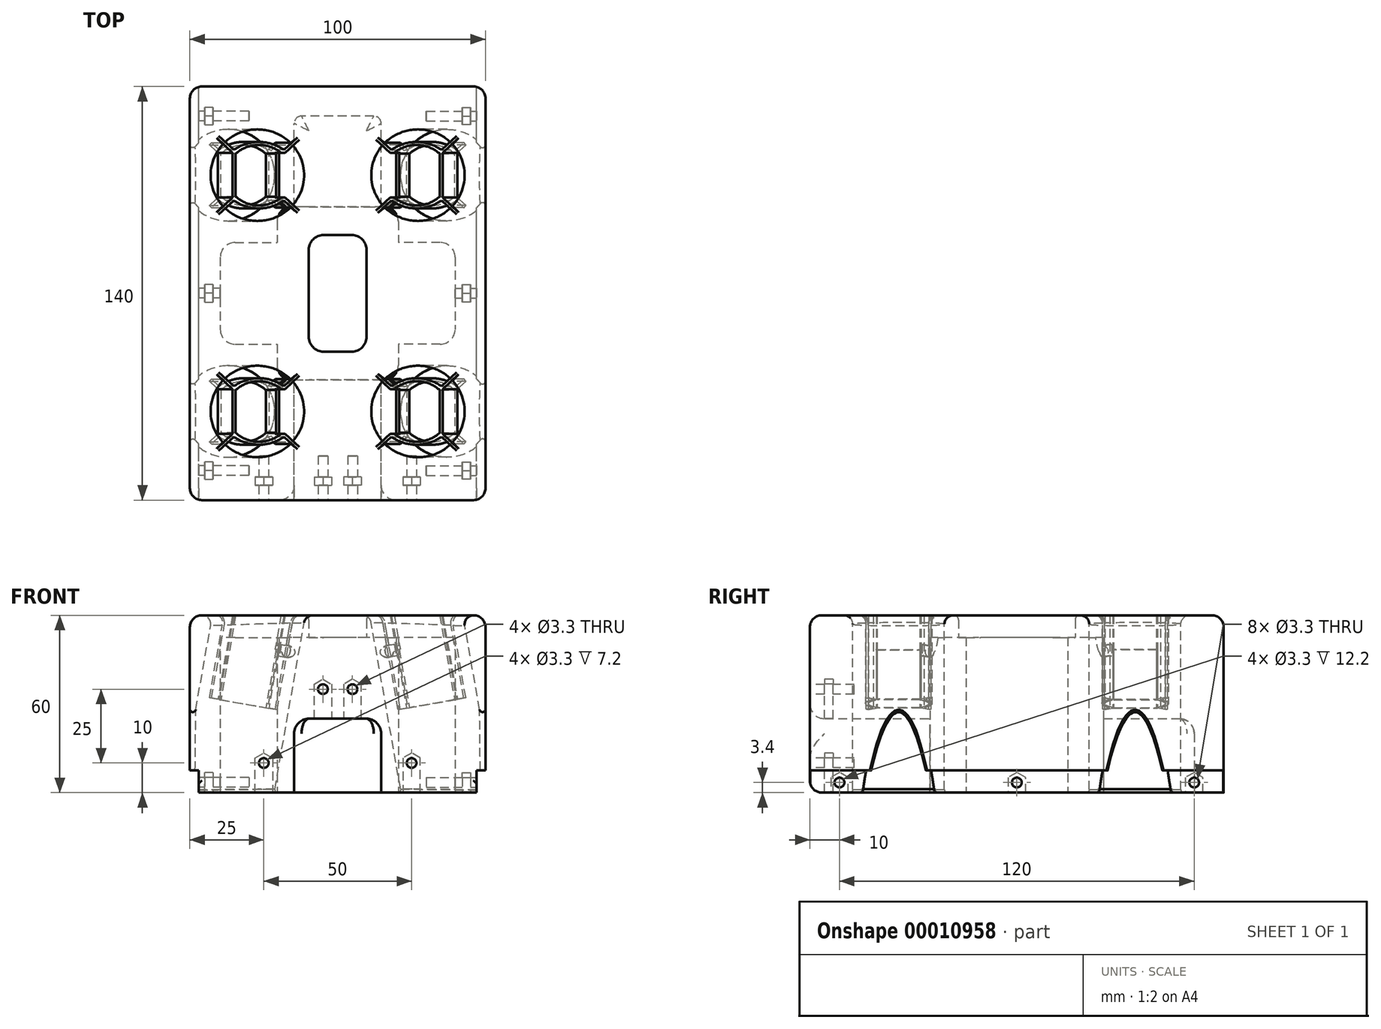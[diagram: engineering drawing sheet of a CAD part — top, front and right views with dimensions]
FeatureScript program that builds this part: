
annotation { "Feature Type Name" : "Feature", "Feature Type Description" : "" }
export const myFeature = defineFeature(function(context is Context, id is Id, definition is map)
    precondition{}
    {
        {
            var Q0;
            Q0=qCreatedBy(makeId("Right.planeOp"),FACE);
            var sketch = newSketch(context, id + "F0", { "sketchPlane" : qUnion([Q0])});
            skLineSegment(sketch, "E0", {"start": v(-70, 30) * mm, "end": v(70, 30) * mm});
            skLineSegment(sketch, "E1", {"start": v(70, 30) * mm, "end": v(70, -30) * mm});
            skLineSegment(sketch, "E2", {"start": v(70, -30) * mm, "end": v(-70, -30) * mm});
            skLineSegment(sketch, "E3", {"start": v(-70, -30) * mm, "end": v(-70, 0) * mm});
            skLineSegment(sketch, "E4", {"start": v(-70, 0) * mm, "end": v(-70, 0) * mm});
            skLineSegment(sketch, "E5", {"start": v(-70, 0) * mm, "end": v(-70, 30) * mm});
            skLineSegment(sketch, "E6", {"start": v(-70, 0) * mm, "end": v(70, 0) * mm, "construction": true});
            skSolve(sketch);
        }
        {
            var Q0;
            Q0=qSketchRegion(id+"F0",true);
            extrude(context, id + "F1", {"entities" : qUnion([Q0]), "depth" : 50 * mm});
        }
        {
            var Q0;
            Q0=qCreatedBy(makeId("Front.planeOp"),FACE);
            var sketch = newSketch(context, id + "F2", { "sketchPlane" : qUnion([Q0])});
            skLineSegment(sketch, "E7", {"start": v(25, -30) * mm, "end": v(25, 30) * mm, "construction": true});
            skLineSegment(sketch, "E8", {"start": v(50, 30) * mm, "end": v(0, 38.82) * mm, "construction": true});
            skLineSegment(sketch, "E9", {"start": v(0, 38.82) * mm, "end": v(-5.12, 9.78) * mm, "construction": true});
            skSolve(sketch);
        }
        {
            var Q0;
            Q0=sQuery(id+"F2.wireOp",EDGE,"E9");
            var Q1;
            Q1=sQuery(id+"F2.wireOp",VERTEX,"E8.end");
            cPlane(context, id + "F3", {"entities" : qUnion([Q0, Q1]), "cplaneType" : CPlaneType.LINE_POINT, "offset" : 150 * mm, "width" : 150 * mm, "height" : 150 * mm});
        }
        {
            var Q0;
            Q0=qCreatedBy(id+"F3.planeOp",FACE);
            cPlane(context, id + "F4", {"entities" : qUnion([Q0]), "cplaneType" : CPlaneType.OFFSET, "offset" : 35 * mm, "width" : 150 * mm, "height" : 150 * mm});
        }
        {
            var Q0;
            Q0=qCreatedBy(id+"F4.planeOp",FACE);
            cPlane(context, id + "F5", {"entities" : qUnion([Q0]), "cplaneType" : CPlaneType.OFFSET, "offset" : 20 * mm, "oppositeDirection" : true, "width" : 150 * mm, "height" : 150 * mm});
        }
        {
            var Q0;
            Q0=qCreatedBy(id+"F3.planeOp",FACE);
            var sketch = newSketch(context, id + "F6", { "sketchPlane" : qUnion([Q0])});
            skCircle(sketch, "E10", {"center": v(17.8, -40) * mm, "radius": 15.5 * mm});
            skCircle(sketch, "E11", {"center": v(17.8, 40) * mm, "radius": 15.5 * mm});
            skLineSegment(sketch, "E12", {"start": v(17.8, -40) * mm, "end": v(17.8, 40) * mm, "construction": true});
            skLineSegment(sketch, "E13", {"start": v(17.8, -40) * mm, "end": v(17.8, -70) * mm, "construction": true});
            skLineSegment(sketch, "E14", {"start": v(17.8, 40) * mm, "end": v(17.8, 70) * mm, "construction": true});
            skSolve(sketch);
        }
        {
            var Q0;
            Q0=qSketchRegion(id+"F6",true);
            extrude(context, id + "F7", {"entities" : qUnion([Q0]), "operationType" : NewBodyOperationType.REMOVE, "endBound" : BoundingType.THROUGH_ALL, "depth" : 25 * mm});
        }
        {
            var Q0;
            Q0=makeQuery(id+"F7.boolean.opBoolean","INTERSECT",EDGE,{"derivedFrom":[makeQuery(id+"F1.opExtrude","CAP_FACE",FACE,{"disambiguationData":[OSD([sQuery(id+"F0.wireOp",EDGE,"E0"),sQuery(id+"F0.wireOp",EDGE,"E1"),sQuery(id+"F0.wireOp",EDGE,"E2"),sQuery(id+"F0.wireOp",EDGE,"E3"),sQuery(id+"F0.wireOp",EDGE,"E4"),sQuery(id+"F0.wireOp",EDGE,"E5")])],"isStart":true}),makeQuery(id+"F7.opExtrude","SWEPT_FACE",FACE,{"disambiguationData":[OSD([sQuery(id+"F6.wireOp",EDGE,"E10")])]})]});
            var Q1;
            Q1=makeQuery(id+"F7.boolean.opBoolean","INTERSECT",EDGE,{"derivedFrom":[makeQuery(id+"F1.opExtrude","CAP_FACE",FACE,{"disambiguationData":[OSD([sQuery(id+"F0.wireOp",EDGE,"E0"),sQuery(id+"F0.wireOp",EDGE,"E1"),sQuery(id+"F0.wireOp",EDGE,"E2"),sQuery(id+"F0.wireOp",EDGE,"E3"),sQuery(id+"F0.wireOp",EDGE,"E4"),sQuery(id+"F0.wireOp",EDGE,"E5")])],"isStart":true}),makeQuery(id+"F7.opExtrude","SWEPT_FACE",FACE,{"disambiguationData":[OSD([sQuery(id+"F6.wireOp",EDGE,"E11")])]})]});
            var Q2;
            Q2=makeQuery(id+"F7.boolean.opBoolean","INTERSECT",EDGE,{"derivedFrom":[makeQuery(id+"F1.opExtrude","SWEPT_FACE",FACE,{"disambiguationData":[OSD([sQuery(id+"F0.wireOp",EDGE,"E2")])]}),makeQuery(id+"F7.opExtrude","SWEPT_FACE",FACE,{"disambiguationData":[OSD([sQuery(id+"F6.wireOp",EDGE,"E10")])]})]});
            var Q3;
            Q3=makeQuery(id+"F7.boolean.opBoolean","INTERSECT",EDGE,{"derivedFrom":[makeQuery(id+"F1.opExtrude","SWEPT_FACE",FACE,{"disambiguationData":[OSD([sQuery(id+"F0.wireOp",EDGE,"E2")])]}),makeQuery(id+"F7.opExtrude","SWEPT_FACE",FACE,{"disambiguationData":[OSD([sQuery(id+"F6.wireOp",EDGE,"E11")])]})]});
            fillet(context, id + "F8", {"entities" : qUnion([Q0, Q1, Q2, Q3]), "radius" : 1 * mm, "tangentPropagation" : true, "allowEdgeOverflow" : false});
        }
        {
            var Q0;
            Q0=qCreatedBy(id+"F4.planeOp",FACE);
            var sketch = newSketch(context, id + "F9", { "sketchPlane" : qUnion([Q0])});
            skLineSegment(sketch, "E15", {"start": v(0, 0) * mm, "end": v(56.92, 0) * mm, "construction": true});
            skCircle(sketch, "E16", {"center": v(17.8, 40) * mm, "radius": 22.72 * mm, "construction": true});
            skLineSegment(sketch, "E17", {"start": v(26.54, 31.75) * mm, "end": v(26.54, 48.25) * mm});
            skLineSegment(sketch, "E18", {"start": v(26.54, 31.75) * mm, "end": v(9.04, 31.75) * mm, "construction": true});
            skLineSegment(sketch, "E19", {"start": v(9.04, 31.75) * mm, "end": v(9.04, 48.25) * mm});
            skLineSegment(sketch, "E20", {"start": v(9.04, 48.25) * mm, "end": v(26.54, 48.25) * mm, "construction": true});
            skArc(sketch, "E21", {"start": v(9.04, 31.75) * mm, "mid": v(17.8, 28.75) * mm, "end": v(26.54, 31.75) * mm});
            skArc(sketch, "E22", {"start": v(26.54, 48.25) * mm, "mid": v(17.8, 51.25) * mm, "end": v(9.04, 48.25) * mm});
            skPoint(sketch, "E23.endSnap0", {"position": v(26.54, 40) * mm});
            skLineSegment(sketch, "E24", {"start": v(26.54, 40) * mm, "end": v(17.8, 40) * mm, "construction": true});
            skLineSegment(sketch, "E25", {"start": v(17.8, 40) * mm, "end": v(9.04, 40) * mm, "construction": true});
            skLineSegment(sketch, "E26", {"start": v(17.8, 28.75) * mm, "end": v(17.8, 51.25) * mm, "construction": true});
            skLineSegment(sketch, "E27", {"start": v(17.8, 40) * mm, "end": v(34.32, 24.41) * mm, "construction": true});
            skLineSegment(sketch, "E28", {"start": v(26.13, 31.45) * mm, "end": v(33.97, 24.05) * mm});
            skLineSegment(sketch, "E29", {"start": v(34.66, 24.78) * mm, "end": v(26.54, 32.44) * mm});
            skLineSegment(sketch, "E30", {"start": v(33.97, 24.05) * mm, "end": v(34.32, 24.42) * mm});
            skLineSegment(sketch, "E31", {"start": v(34.32, 24.42) * mm, "end": v(34.66, 24.78) * mm});
            skLineSegment(sketch, "E32", {"start": v(26.54, 40) * mm, "end": v(40.5, 40) * mm, "construction": true});
            skLineSegment(sketch, "E33.MirrorCS", {"start": v(34.32, 55.58) * mm, "end": v(34.66, 55.22) * mm});
            skLineSegment(sketch, "E34.MirrorCS", {"start": v(33.97, 55.95) * mm, "end": v(34.32, 55.58) * mm});
            skLineSegment(sketch, "E35.MirrorCS", {"start": v(34.66, 55.22) * mm, "end": v(26.54, 47.56) * mm});
            skLineSegment(sketch, "E36.MirrorCS", {"start": v(26.13, 48.55) * mm, "end": v(33.97, 55.95) * mm});
            skLineSegment(sketch, "E37.MirrorCS", {"start": v(9.45, 48.55) * mm, "end": v(1.6, 55.95) * mm});
            skLineSegment(sketch, "E38.MirrorCS", {"start": v(0.92, 55.22) * mm, "end": v(9.04, 47.56) * mm});
            skLineSegment(sketch, "E39.MirrorCS", {"start": v(1.6, 55.95) * mm, "end": v(1.26, 55.58) * mm});
            skLineSegment(sketch, "E40.MirrorCS", {"start": v(1.26, 55.58) * mm, "end": v(0.92, 55.22) * mm});
            skLineSegment(sketch, "E41.MirrorCS", {"start": v(9.45, 31.45) * mm, "end": v(1.6, 24.05) * mm});
            skLineSegment(sketch, "E42.MirrorCS", {"start": v(0.92, 24.78) * mm, "end": v(9.04, 32.44) * mm});
            skLineSegment(sketch, "E43.MirrorCS", {"start": v(1.26, 24.42) * mm, "end": v(0.92, 24.78) * mm});
            skLineSegment(sketch, "E44.MirrorCS", {"start": v(1.6, 24.05) * mm, "end": v(1.26, 24.42) * mm});
            skLineSegment(sketch, "E45.MirrorCS", {"start": v(34.32, -24.42) * mm, "end": v(34.66, -24.78) * mm});
            skLineSegment(sketch, "E46.MirrorCS", {"start": v(33.97, -24.05) * mm, "end": v(34.32, -24.42) * mm});
            skLineSegment(sketch, "E47.MirrorCS", {"start": v(1.6, -55.95) * mm, "end": v(1.26, -55.58) * mm});
            skLineSegment(sketch, "E48.MirrorCS", {"start": v(1.26, -55.58) * mm, "end": v(0.92, -55.22) * mm});
            skLineSegment(sketch, "E49.MirrorCS", {"start": v(1.26, -24.42) * mm, "end": v(0.92, -24.78) * mm});
            skLineSegment(sketch, "E50.MirrorCS", {"start": v(1.6, -24.05) * mm, "end": v(1.26, -24.42) * mm});
            skLineSegment(sketch, "E51.MirrorCS", {"start": v(33.97, -55.95) * mm, "end": v(34.32, -55.58) * mm});
            skLineSegment(sketch, "E52.MirrorCS", {"start": v(34.32, -55.58) * mm, "end": v(34.66, -55.22) * mm});
            skLineSegment(sketch, "E53.MirrorCS", {"start": v(17.8, -40) * mm, "end": v(34.32, -24.41) * mm, "construction": true});
            skLineSegment(sketch, "E54.MirrorCS", {"start": v(26.54, -40) * mm, "end": v(17.8, -40) * mm, "construction": true});
            skLineSegment(sketch, "E55.MirrorCS", {"start": v(26.54, -31.75) * mm, "end": v(26.54, -48.25) * mm});
            skLineSegment(sketch, "E56.MirrorCS", {"start": v(9.04, -31.75) * mm, "end": v(9.04, -48.25) * mm});
            skLineSegment(sketch, "E57.MirrorCS", {"start": v(0.92, -24.78) * mm, "end": v(9.04, -32.44) * mm});
            skLineSegment(sketch, "E58.MirrorCS", {"start": v(26.54, -40) * mm, "end": v(40.5, -40) * mm});
            skArc(sketch, "E59.MirrorCS", {"start": v(9.04, -31.75) * mm, "mid": v(17.8, -28.75) * mm, "end": v(26.54, -31.75) * mm});
            skLineSegment(sketch, "E60.MirrorCS", {"start": v(34.66, -55.22) * mm, "end": v(26.54, -47.56) * mm});
            skLineSegment(sketch, "E61.MirrorCS", {"start": v(9.45, -31.45) * mm, "end": v(1.6, -24.05) * mm});
            skLineSegment(sketch, "E62.MirrorCS", {"start": v(17.8, -28.75) * mm, "end": v(17.8, -51.25) * mm, "construction": true});
            skArc(sketch, "E63.MirrorCS", {"start": v(26.54, -48.25) * mm, "mid": v(17.8, -51.25) * mm, "end": v(9.04, -48.25) * mm});
            skLineSegment(sketch, "E64.MirrorCS", {"start": v(9.04, -48.25) * mm, "end": v(26.54, -48.25) * mm, "construction": true});
            skLineSegment(sketch, "E65.MirrorCS", {"start": v(9.45, -48.55) * mm, "end": v(1.6, -55.95) * mm});
            skLineSegment(sketch, "E66.MirrorCS", {"start": v(26.13, -31.45) * mm, "end": v(33.97, -24.05) * mm});
            skCircle(sketch, "E67.MirrorC", {"center": v(17.8, -40) * mm, "radius": 22.72 * mm, "construction": true});
            skLineSegment(sketch, "E68.MirrorCS", {"start": v(0.92, -55.22) * mm, "end": v(9.04, -47.56) * mm});
            skLineSegment(sketch, "E69.MirrorCS", {"start": v(17.8, -40) * mm, "end": v(9.04, -40) * mm, "construction": true});
            skLineSegment(sketch, "E70.MirrorCS", {"start": v(26.13, -48.55) * mm, "end": v(33.97, -55.95) * mm});
            skLineSegment(sketch, "E71.MirrorCS", {"start": v(34.66, -24.78) * mm, "end": v(26.54, -32.44) * mm});
            skPoint(sketch, "E72.MirrorP", {"position": v(26.54, -40) * mm});
            skLineSegment(sketch, "E73.MirrorCS", {"start": v(26.54, -31.75) * mm, "end": v(9.04, -31.75) * mm, "construction": true});
            skSolve(sketch);
        }
        {
            var Q0;
            {var subQ5=sQuery(id+"F9.wireOp",EDGE,"E17");var subQ9=sQuery(id+"F9.wireOp",EDGE,"E21");var subQ10=makeQuery(id+"F9.imprint","INTERSECT",VERTEX,{"derivedFrom":[subQ5,subQ9]});Q0=makeQuery(id+"F9.imprint","IMPRINT",FACE,{"disambiguationData":[TD([[makeQuery(id+"F9.imprint","IMPRINT",EDGE,{"disambiguationData":[TD([[subQ10,-1.0]])],"derivedFrom":subQ5}),1.0]])]});}
            var Q1;
            {var subQ4=sQuery(id+"F9.wireOp",EDGE,"E28");Q1=makeQuery(id+"F9.imprint","IMPRINT",FACE,{"disambiguationData":[TD([[makeQuery(id+"F9.imprint","IMPRINT",EDGE,{"derivedFrom":subQ4}),1.0]])]});}
            var Q2;
            Q2=makeQuery(id+"F9.imprint","IMPRINT",FACE,{"disambiguationData":[TD([[makeQuery(id+"F9.imprint","IMPRINT",EDGE,{"derivedFrom":sQuery(id+"F9.wireOp",EDGE,"E33.MirrorCS")}),-1.0]])]});
            var Q3;
            {var subQ4=sQuery(id+"F9.wireOp",EDGE,"E41.MirrorCS");Q3=makeQuery(id+"F9.imprint","IMPRINT",FACE,{"disambiguationData":[TD([[makeQuery(id+"F9.imprint","IMPRINT",EDGE,{"derivedFrom":subQ4}),-1.0]])]});}
            var Q4;
            {var subQ4=sQuery(id+"F9.wireOp",EDGE,"E37.MirrorCS");Q4=makeQuery(id+"F9.imprint","IMPRINT",FACE,{"disambiguationData":[TD([[makeQuery(id+"F9.imprint","IMPRINT",EDGE,{"derivedFrom":subQ4}),1.0]])]});}
            var Q5;
            {var subQ5=sQuery(id+"F9.wireOp",EDGE,"E55.MirrorCS");var subQ10=makeQuery(id+"F9.imprint","IMPRINT",VERTEX,{"derivedFrom":subQ5});Q5=makeQuery(id+"F9.imprint","IMPRINT",FACE,{"disambiguationData":[TD([[makeQuery(id+"F9.imprint","IMPRINT",EDGE,{"disambiguationData":[TD([[subQ10,1.0]])],"derivedFrom":subQ5}),-1.0]])]});}
            var Q6;
            Q6=makeQuery(id+"F9.imprint","IMPRINT",FACE,{"disambiguationData":[TD([[makeQuery(id+"F9.imprint","IMPRINT",EDGE,{"derivedFrom":sQuery(id+"F9.wireOp",EDGE,"E45.MirrorCS")}),-1.0]])]});
            var Q7;
            Q7=makeQuery(id+"F9.imprint","IMPRINT",FACE,{"disambiguationData":[TD([[makeQuery(id+"F9.imprint","IMPRINT",EDGE,{"derivedFrom":sQuery(id+"F9.wireOp",EDGE,"E49.MirrorCS")}),1.0]])]});
            var Q8;
            Q8=makeQuery(id+"F9.imprint","IMPRINT",FACE,{"disambiguationData":[TD([[makeQuery(id+"F9.imprint","IMPRINT",EDGE,{"derivedFrom":sQuery(id+"F9.wireOp",EDGE,"E48.MirrorCS")}),-1.0]])]});
            var Q9;
            Q9=makeQuery(id+"F9.imprint","IMPRINT",FACE,{"disambiguationData":[TD([[makeQuery(id+"F9.imprint","IMPRINT",EDGE,{"derivedFrom":sQuery(id+"F9.wireOp",EDGE,"E51.MirrorCS")}),1.0]])]});
            var Q10;
            Q10=makeQuery(id+"F1.opExtrude","SWEPT_FACE",FACE,{"disambiguationData":[OSD([sQuery(id+"F0.wireOp",EDGE,"E0")])]});
            extrude(context, id + "F10", {"entities" : qUnion([Q0, Q1, Q2, Q3, Q4, Q5, Q6, Q7, Q8, Q9]), "operationType" : NewBodyOperationType.ADD, "endBound" : BoundingType.UP_TO_SURFACE, "oppositeDirection" : true, "endBoundEntityFace" : qUnion([Q10]), "depth" : 3 * mm});
        }
        {
            var Q0;
            Q0=qCreatedBy(id+"F4.planeOp",FACE);
            var sketch = newSketch(context, id + "F11", { "sketchPlane" : qUnion([Q0])});
            skLineSegment(sketch, "E74", {"start": v(0, 0) * mm, "end": v(45.33, 0) * mm, "construction": true});
            skLineSegment(sketch, "E75.bottom", {"start": v(25.54, 32.75) * mm, "end": v(10.04, 32.75) * mm, "construction": true});
            skLineSegment(sketch, "E75.top", {"start": v(25.54, 47.25) * mm, "end": v(10.04, 47.25) * mm, "construction": true});
            skLineSegment(sketch, "E75.left", {"start": v(25.54, 32.75) * mm, "end": v(25.54, 47.25) * mm});
            skLineSegment(sketch, "E75.right", {"start": v(10.04, 32.75) * mm, "end": v(10.04, 47.25) * mm});
            skLineSegment(sketch, "E76", {"start": v(17.8, 32.75) * mm, "end": v(17.8, 40) * mm, "construction": true});
            skLineSegment(sketch, "E77", {"start": v(17.8, 40) * mm, "end": v(17.8, 47.25) * mm, "construction": true});
            skArc(sketch, "E78", {"start": v(10.04, 32.75) * mm, "mid": v(17.8, 29.75) * mm, "end": v(25.54, 32.75) * mm});
            skArc(sketch, "E79", {"start": v(25.54, 47.25) * mm, "mid": v(17.8, 50.25) * mm, "end": v(10.04, 47.25) * mm});
            skArc(sketch, "E80.MirrorCS", {"start": v(10.04, -32.75) * mm, "mid": v(17.8, -29.75) * mm, "end": v(25.54, -32.75) * mm});
            skArc(sketch, "E81.MirrorCS", {"start": v(25.54, -47.25) * mm, "mid": v(17.8, -50.25) * mm, "end": v(10.04, -47.25) * mm});
            skLineSegment(sketch, "E82.MirrorCS", {"start": v(17.8, -40) * mm, "end": v(17.8, -47.25) * mm});
            skLineSegment(sketch, "E83.MirrorCS", {"start": v(25.54, -32.75) * mm, "end": v(10.04, -32.75) * mm});
            skLineSegment(sketch, "E84.MirrorCS", {"start": v(25.54, -47.25) * mm, "end": v(10.04, -47.25) * mm});
            skLineSegment(sketch, "E85.MirrorCS", {"start": v(25.54, -32.75) * mm, "end": v(25.54, -47.25) * mm});
            skLineSegment(sketch, "E86.MirrorCS", {"start": v(10.04, -32.75) * mm, "end": v(10.04, -47.25) * mm});
            skLineSegment(sketch, "E87.MirrorCS", {"start": v(17.8, -32.75) * mm, "end": v(17.8, -40) * mm});
            skSolve(sketch);
        }
        {
            var Q0;
            Q0=qSketchRegion(id+"F11",true);
            var Q1;
            {var subQ0=makeQuery(id+"F10.boolean.opBoolean","MERGE",FACE,{"derivedFrom":[makeQuery(id+"F1.opExtrude","SWEPT_FACE",FACE,{"disambiguationData":[OSD([sQuery(id+"F0.wireOp",EDGE,"E0")])]}),makeQuery(id+"F10.opExtrude","CAP_FACE",FACE,{"disambiguationData":[OSD([sQuery(id+"F9.wireOp",EDGE,"5d13eab4-1163-46bd-b668-966f67677cda"),sQuery(id+"F9.wireOp",EDGE,"4a8f1ae0-6c1c-415b-9699-5f4a353e01b7"),sQuery(id+"F9.wireOp",EDGE,"093ffe32-b858-4e39-8033-2af8f1862302"),sQuery(id+"F9.wireOp",EDGE,"6615f876-654d-472b-932f-aa817a99cf8c"),sQuery(id+"F9.wireOp",EDGE,"1d3078c9-2719-406d-bf5a-1ff6bce521da"),sQuery(id+"F9.wireOp",EDGE,"880e6486-e846-4002-b9b7-1cb835c84523"),sQuery(id+"F9.wireOp",EDGE,"7e94aab6-89b0-44ac-a5a2-104160a8799a"),sQuery(id+"F9.wireOp",EDGE,"5bf2236a-818f-4daa-bb11-a80a7fe0e66a"),sQuery(id+"F9.wireOp",EDGE,"dcff3f73-e1ff-4264-9410-abdb107e6245"),sQuery(id+"F9.wireOp",EDGE,"66e4b800-3c0e-4def-9d8a-5724071b2d4d"),sQuery(id+"F9.wireOp",EDGE,"07cf7429-5678-4c4a-b063-5e15791e93b6"),sQuery(id+"F9.wireOp",EDGE,"e1dbcd6d-4689-40e3-8967-04de52220fc4"),sQuery(id+"F9.wireOp",EDGE,"f96e3a45-2d0c-4d7f-8c63-5261d2a80a69.6.MirrorCS"),sQuery(id+"F9.wireOp",EDGE,"f96e3a45-2d0c-4d7f-8c63-5261d2a80a69.10.MirrorCS"),sQuery(id+"F9.wireOp",EDGE,"f96e3a45-2d0c-4d7f-8c63-5261d2a80a69.12.MirrorCS"),sQuery(id+"F9.wireOp",EDGE,"f96e3a45-2d0c-4d7f-8c63-5261d2a80a69.15.MirrorCS"),sQuery(id+"F9.wireOp",EDGE,"f96e3a45-2d0c-4d7f-8c63-5261d2a80a69.17.MirrorCS"),sQuery(id+"F9.wireOp",EDGE,"f96e3a45-2d0c-4d7f-8c63-5261d2a80a69.19.MirrorCS"),sQuery(id+"F9.wireOp",EDGE,"f96e3a45-2d0c-4d7f-8c63-5261d2a80a69.20.MirrorCS"),sQuery(id+"F9.wireOp",EDGE,"f96e3a45-2d0c-4d7f-8c63-5261d2a80a69.22.MirrorCS"),sQuery(id+"F9.wireOp",EDGE,"f96e3a45-2d0c-4d7f-8c63-5261d2a80a69.23.MirrorCS"),sQuery(id+"F9.wireOp",EDGE,"f96e3a45-2d0c-4d7f-8c63-5261d2a80a69.24.MirrorCS"),sQuery(id+"F9.wireOp",EDGE,"f96e3a45-2d0c-4d7f-8c63-5261d2a80a69.26.MirrorCS"),sQuery(id+"F9.wireOp",EDGE,"f96e3a45-2d0c-4d7f-8c63-5261d2a80a69.27.MirrorCS")])],"isStart":false})]});Q1=makeQuery(id+"F42.boolean.opBoolean","MERGE",FACE,{"derivedFrom":[subQ0,makeQuery(id+"F42.opPattern","COPY",FACE,{"derivedFrom":subQ0,"instanceName":"1"})]});}
            extrude(context, id + "F12", {"entities" : qUnion([Q0]), "operationType" : NewBodyOperationType.REMOVE, "endBound" : BoundingType.UP_TO_SURFACE, "oppositeDirection" : true, "endBoundEntityFace" : qUnion([Q1]), "depth" : 25 * mm});
        }
        {
            var Q0;
            Q0=makeQuery(id+"F1.opExtrude","SWEPT_FACE",FACE,{"disambiguationData":[OSD([sQuery(id+"F0.wireOp",EDGE,"E2")])]});
            var sketch = newSketch(context, id + "F13", { "sketchPlane" : qUnion([Q0])});
            skLineSegment(sketch, "E88", {"start": v(12.95, 40) * mm, "end": v(12.95, -40) * mm, "construction": true});
            skLineSegment(sketch, "E89", {"start": v(50, 0) * mm, "end": v(12.95, 0) * mm, "construction": true});
            skLineSegment(sketch, "E90.left", {"start": v(50, -29.33) * mm, "end": v(50, 29.33) * mm});
            skLineSegment(sketch, "E91", {"start": v(50, -29.33) * mm, "end": v(34.5, -29.33) * mm});
            skLineSegment(sketch, "E92", {"start": v(29.5, -24.33) * mm, "end": v(29.5, -17.22) * mm});
            skLineSegment(sketch, "E93", {"start": v(34.5, 29.33) * mm, "end": v(50, 29.33) * mm});
            skPoint(sketch, "E94.visualSharp", {"position": v(29.5, -29.33) * mm});
            skArc(sketch, "E94.filletArc", {"start": v(29.5, -24.33) * mm, "mid": v(30.95, -27.86) * mm, "end": v(34.5, -29.33) * mm});
            skPoint(sketch, "E95.visualSharp", {"position": v(29.5, 29.33) * mm});
            skArc(sketch, "E95.filletArc", {"start": v(34.5, 29.33) * mm, "mid": v(30.95, 27.86) * mm, "end": v(29.5, 24.33) * mm});
            skLineSegment(sketch, "E96.bottom", {"start": v(15.3, -17.22) * mm, "end": v(29.5, -17.22) * mm});
            skLineSegment(sketch, "E96.top", {"start": v(15.3, 17.22) * mm, "end": v(29.5, 17.22) * mm});
            skLineSegment(sketch, "E96.left", {"start": v(10.3, -12.22) * mm, "end": v(10.3, 12.22) * mm});
            skLineSegment(sketch, "E97", {"start": v(0, 0) * mm, "end": v(10.3, 0) * mm, "construction": true});
            skPoint(sketch, "E98.visualSharp", {"position": v(10.3, -17.22) * mm});
            skArc(sketch, "E98.filletArc", {"start": v(10.3, -12.22) * mm, "mid": v(11.76, -15.75) * mm, "end": v(15.3, -17.22) * mm});
            skPoint(sketch, "E99.visualSharp", {"position": v(10.3, 17.22) * mm});
            skArc(sketch, "E99.filletArc", {"start": v(15.3, 17.22) * mm, "mid": v(11.76, 15.75) * mm, "end": v(10.3, 12.22) * mm});
            skLineSegment(sketch, "E100.trimOffspring", {"start": v(29.5, 17.22) * mm, "end": v(29.5, 24.33) * mm});
            skSolve(sketch);
        }
        {
            var Q0;
            Q0=qSketchRegion(id+"F13",true);
            extrude(context, id + "F14", {"entities" : qUnion([Q0]), "operationType" : NewBodyOperationType.REMOVE, "oppositeDirection" : true, "depth" : 52.5 * mm});
        }
        {
            var Q0;
            Q0=sQuery(id+"F9.wireOp",EDGE,"E27");
            var Q1;
            Q1=sQuery(id+"F9.wireOp",VERTEX,"E31.start");
            cPlane(context, id + "F15", {"entities" : qUnion([Q0, Q1]), "cplaneType" : CPlaneType.CURVE_POINT, "offset" : 150 * mm, "width" : 150 * mm, "height" : 150 * mm});
        }
        {
            var Q0;
            Q0=qCreatedBy(id+"F15.planeOp",FACE);
            var sketch = newSketch(context, id + "F16", { "sketchPlane" : qUnion([Q0])});
            skCircle(sketch, "E101", {"center": v(-41.3, 23.23) * mm, "radius": 2 * mm});
            skLineSegment(sketch, "E102", {"start": v(-41.3, 3.23) * mm, "end": v(-41.3, 23.23) * mm, "construction": true});
            skSolve(sketch);
        }
        {
            var Q0;
            Q0 = qSketchRegion(id + "F16", true);
            var Q1;
            Q1=makeQuery(id+"F10.opExtrude","SWEPT_FACE",FACE,{"disambiguationData":[OSD([sQuery(id+"F9.wireOp",EDGE,"E21")])]});
            extrude(context, id + "F17", {"entities" : qUnion([Q0]), "endBound" : BoundingType.UP_TO_SURFACE, "oppositeDirection" : true, "endBoundEntityFace" : qUnion([Q1]), "depth" : 10.65 * mm});
        }
        {
            var Q0;
            Q0=makeQuery(id+"F17.opExtrude","SWEPT_BODY",BODY,{"disambiguationData":[OSD([sQuery(id+"F16.wireOp",EDGE,"E101")])]});
            var Q1;
            Q1=qCreatedBy(makeId("Front.planeOp"),FACE);
            mirror(context, id + "F18", {"entities" : qUnion([Q0]), "mirrorPlane" : qUnion([Q1])});
        }
        {
            var Q0;
            Q0=makeQuery(id+"F18.opPattern","COPY",BODY,{"derivedFrom":makeQuery(id+"F17.opExtrude","SWEPT_BODY",BODY,{"disambiguationData":[OSD([sQuery(id+"F16.wireOp",EDGE,"E101")])]}),"instanceName":"1"});
            var Q1;
            Q1=makeQuery(id+"F17.opExtrude","SWEPT_BODY",BODY,{"disambiguationData":[OSD([sQuery(id+"F16.wireOp",EDGE,"E101")])]});
            var Q2;
            Q2=makeQuery(id+"F1.opExtrude","SWEPT_BODY",BODY,{"disambiguationData":[OSD([sQuery(id+"F0.wireOp",EDGE,"E0"),sQuery(id+"F0.wireOp",EDGE,"E1"),sQuery(id+"F0.wireOp",EDGE,"E2"),sQuery(id+"F0.wireOp",EDGE,"E3"),sQuery(id+"F0.wireOp",EDGE,"E5")])]});
            booleanBodies(context, id + "F19", {"operationType" : BooleanOperationType.SUBTRACTION, "tools" : qUnion([Q0, Q1]), "targets" : qUnion([Q2])});
        }
        {
            var Q0;
            Q0=qCreatedBy(id+"F5.planeOp",FACE);
            var sketch = newSketch(context, id + "F20", { "sketchPlane" : qUnion([Q0])});
            skLineSegment(sketch, "E103.bottom", {"start": v(26.54, 47.56) * mm, "end": v(24.14, 47.56) * mm});
            skLineSegment(sketch, "E103.top", {"start": v(26.54, 32.44) * mm, "end": v(24.14, 32.44) * mm});
            skLineSegment(sketch, "E103.left", {"start": v(26.54, 47.56) * mm, "end": v(26.54, 32.44) * mm});
            skLineSegment(sketch, "E103.right", {"start": v(24.14, 47.56) * mm, "end": v(24.14, 32.44) * mm});
            skPoint(sketch, "E104", {"position": v(20.4, 0) * mm});
            skLineSegment(sketch, "E105", {"start": v(7.55, 0) * mm, "end": v(20.4, 0) * mm, "construction": true});
            skLineSegment(sketch, "E106", {"start": v(20.4, -24.72) * mm, "end": v(20.4, 24.72) * mm, "construction": true});
            skLineSegment(sketch, "E107.MirrorCS", {"start": v(26.54, -47.56) * mm, "end": v(24.14, -47.56) * mm});
            skLineSegment(sketch, "E108.MirrorCS", {"start": v(26.54, -32.44) * mm, "end": v(24.14, -32.44) * mm});
            skLineSegment(sketch, "E109.MirrorCS", {"start": v(26.54, -47.56) * mm, "end": v(26.54, -32.44) * mm});
            skLineSegment(sketch, "E110.MirrorCS", {"start": v(24.14, -47.56) * mm, "end": v(24.14, -32.44) * mm});
            skSolve(sketch);
        }
        {
            var Q0;
            Q0=qSketchRegion(id+"F20",true);
            extrude(context, id + "F21", {"entities" : qUnion([Q0]), "operationType" : NewBodyOperationType.REMOVE, "endBound" : BoundingType.THROUGH_ALL, "oppositeDirection" : true, "depth" : 10 * mm});
        }
        {
            var Q0;
            {var subQ0=makeQuery(id+"F1.opExtrude","SWEPT_FACE",FACE,{"disambiguationData":[OSD([sQuery(id+"F0.wireOp",EDGE,"E2")])]});Q0=makeQuery(id+"F42.boolean.opBoolean","MERGE",FACE,{"derivedFrom":[subQ0,makeQuery(id+"F42.opPattern","COPY",FACE,{"derivedFrom":subQ0,"instanceName":"1"})]});}
            var sketch = newSketch(context, id + "F22", { "sketchPlane" : qUnion([Q0])});
            skLineSegment(sketch, "E111.bottom", {"start": v(50.28, 81.73) * mm, "end": v(37.78, 81.73) * mm});
            skLineSegment(sketch, "E111.top", {"start": v(50.28, -60) * mm, "end": v(37.78, -60) * mm});
            skLineSegment(sketch, "E111.left", {"start": v(50.28, 81.73) * mm, "end": v(50.28, -60) * mm});
            skLineSegment(sketch, "E111.right", {"start": v(35.28, 79.23) * mm, "end": v(35.28, -57.5) * mm});
            skPoint(sketch, "E112.visualSharp", {"position": v(35.28, 81.73) * mm});
            skArc(sketch, "E112.filletArc", {"start": v(37.78, 81.73) * mm, "mid": v(36.02, 81) * mm, "end": v(35.28, 79.23) * mm});
            skPoint(sketch, "E113.visualSharp", {"position": v(35.28, -60) * mm});
            skArc(sketch, "E113.filletArc", {"start": v(35.28, -57.5) * mm, "mid": v(36.02, -59.27) * mm, "end": v(37.78, -60) * mm});
            skLineSegment(sketch, "E114", {"start": v(42.5, 0) * mm, "end": v(0, 0) * mm, "construction": true});
            skSolve(sketch);
        }
        {
            var Q0;
            Q0=qSketchRegion(id+"F22",true);
            extrude(context, id + "F23", {"entities" : qUnion([Q0]), "operationType" : NewBodyOperationType.REMOVE, "oppositeDirection" : true, "depth" : 25 * mm});
        }
        {
            var Q0;
            Q0=makeQuery(id+"F14.boolean.opBoolean","COPY",FACE,{"derivedFrom":makeQuery(id+"F14.opExtrude","CAP_FACE",FACE,{"disambiguationData":[OSD([sQuery(id+"F13.wireOp",EDGE,"E90.left"),sQuery(id+"F13.wireOp",EDGE,"E91"),sQuery(id+"F13.wireOp",EDGE,"E92"),sQuery(id+"F13.wireOp",EDGE,"E93"),sQuery(id+"F13.wireOp",EDGE,"E94.filletArc"),sQuery(id+"F13.wireOp",EDGE,"E95.filletArc"),sQuery(id+"F13.wireOp",EDGE,"E96.bottom"),sQuery(id+"F13.wireOp",EDGE,"E96.top"),sQuery(id+"F13.wireOp",EDGE,"E96.left"),sQuery(id+"F13.wireOp",EDGE,"E98.filletArc"),sQuery(id+"F13.wireOp",EDGE,"E99.filletArc"),sQuery(id+"F13.wireOp",EDGE,"E100.trimOffspring")])],"isStart":false})});
            var sketch = newSketch(context, id + "F24", { "sketchPlane" : qUnion([Q0])});
            skLineSegment(sketch, "E115.bottom", {"start": v(50, -19.73) * mm, "end": v(45.22, -19.73) * mm});
            skLineSegment(sketch, "E115.top", {"start": v(50, 19.73) * mm, "end": v(45.22, 19.73) * mm});
            skLineSegment(sketch, "E115.left", {"start": v(50, -19.73) * mm, "end": v(50, 19.73) * mm});
            skLineSegment(sketch, "E115.right", {"start": v(40.22, -14.73) * mm, "end": v(40.22, 14.73) * mm});
            skPoint(sketch, "E116.visualSharp", {"position": v(40.22, 19.73) * mm});
            skArc(sketch, "E116.filletArc", {"start": v(45.22, 19.73) * mm, "mid": v(41.69, 18.27) * mm, "end": v(40.22, 14.73) * mm});
            skPoint(sketch, "E117.visualSharp", {"position": v(40.22, -19.73) * mm});
            skArc(sketch, "E117.filletArc", {"start": v(40.22, -14.73) * mm, "mid": v(41.69, -18.27) * mm, "end": v(45.22, -19.73) * mm});
            skLineSegment(sketch, "E118", {"start": v(40.22, 0) * mm, "end": v(50, 0) * mm, "construction": true});
            skSolve(sketch);
        }
        {
            var Q0;
            Q0=qSketchRegion(id+"F24",true);
            extrude(context, id + "F25", {"entities" : qUnion([Q0]), "operationType" : NewBodyOperationType.REMOVE, "endBound" : BoundingType.THROUGH_ALL, "oppositeDirection" : true, "depth" : 25 * mm});
        }
        {
            var Q0;
            Q0=makeQuery(id+"F23.boolean.opBoolean","COPY",EDGE,{"disambiguationData":[OD(1.0)],"derivedFrom":makeQuery(id+"F23.opExtrude","CAP_EDGE",EDGE,{"disambiguationData":[OSD([sQuery(id+"F22.wireOp",EDGE,"E111.right")])],"isStart":false})});
            var Q1;
            Q1=makeQuery(id+"F42.opPattern","COPY",EDGE,{"derivedFrom":makeQuery(id+"F23.boolean.opBoolean","COPY",EDGE,{"disambiguationData":[OD(1.0)],"derivedFrom":makeQuery(id+"F23.opExtrude","CAP_EDGE",EDGE,{"disambiguationData":[OSD([sQuery(id+"F22.wireOp",EDGE,"E111.right")])],"isStart":false})}),"instanceName":"1"});
            var Q2;
            {var subQ0=makeQuery(id+"F23.boolean.opBoolean","INTERSECT",EDGE,{"derivedFrom":[makeQuery(id+"F1.opExtrude","SWEPT_FACE",FACE,{"disambiguationData":[OSD([sQuery(id+"F0.wireOp",EDGE,"E3"),sQuery(id+"F0.wireOp",EDGE,"E5")])]}),makeQuery(id+"F23.opExtrude","CAP_FACE",FACE,{"disambiguationData":[OSD([sQuery(id+"F22.wireOp",EDGE,"E111.bottom"),sQuery(id+"F22.wireOp",EDGE,"E111.top"),sQuery(id+"F22.wireOp",EDGE,"E111.left"),sQuery(id+"F22.wireOp",EDGE,"E111.right"),sQuery(id+"F22.wireOp",EDGE,"E112.filletArc"),sQuery(id+"F22.wireOp",EDGE,"E113.filletArc")])],"isStart":false})]});Q2=makeQuery(id+"F42.boolean.opBoolean","MERGE",EDGE,{"derivedFrom":[subQ0,makeQuery(id+"F42.opPattern","COPY",EDGE,{"derivedFrom":subQ0,"instanceName":"1"})]});}
            var Q3;
            Q3=makeQuery(id+"F42.opPattern","COPY",EDGE,{"derivedFrom":makeQuery(id+"F23.boolean.opBoolean","INTERSECT",EDGE,{"derivedFrom":[makeQuery(id+"F1.opExtrude","SWEPT_FACE",FACE,{"disambiguationData":[OSD([sQuery(id+"F0.wireOp",EDGE,"E3"),sQuery(id+"F0.wireOp",EDGE,"E5")])]}),makeQuery(id+"F23.opExtrude","SWEPT_FACE",FACE,{"disambiguationData":[OSD([sQuery(id+"F22.wireOp",EDGE,"E111.right")])]})]}),"instanceName":"1"});
            fillet(context, id + "F26", {"entities" : qUnion([Q0, Q1, Q2, Q3]), "radius" : 5 * mm, "tangentPropagation" : true, "allowEdgeOverflow" : false});
        }
        {
            var Q0;
            Q0=makeQuery(id+"F1.opExtrude","CAP_FACE",FACE,{"disambiguationData":[OSD([sQuery(id+"F0.wireOp",EDGE,"E0"),sQuery(id+"F0.wireOp",EDGE,"E1"),sQuery(id+"F0.wireOp",EDGE,"E2"),sQuery(id+"F0.wireOp",EDGE,"E3"),sQuery(id+"F0.wireOp",EDGE,"E5")])],"isStart":true});
            var sketch = newSketch(context, id + "F27", { "sketchPlane" : qUnion([Q0])});
            skCircle(sketch, "E119", {"center": v(60, -26.6) * mm, "radius": 1.65 * mm});
            skCircle(sketch, "E120", {"center": v(0, -26.6) * mm, "radius": 1.65 * mm});
            skCircle(sketch, "E121", {"center": v(-60, -26.6) * mm, "radius": 1.65 * mm});
            skLineSegment(sketch, "E122", {"start": v(60, -26.6) * mm, "end": v(0, -26.6) * mm, "construction": true});
            skLineSegment(sketch, "E123", {"start": v(0, -26.6) * mm, "end": v(0, -26.6) * mm});
            skLineSegment(sketch, "E124", {"start": v(0, -26.6) * mm, "end": v(-60, -26.6) * mm, "construction": true});
            skLineSegment(sketch, "E125", {"start": v(0, 0) * mm, "end": v(0, -26.6) * mm, "construction": true});
            skSolve(sketch);
        }
        {
            var Q0;
            Q0=qSketchRegion(id+"F27",true);
            extrude(context, id + "F28", {"entities" : qUnion([Q0]), "operationType" : NewBodyOperationType.REMOVE, "oppositeDirection" : true, "depth" : 20 * mm});
        }
        {
            var Q0;
            Q0=makeQuery(id+"F1.opExtrude","CAP_FACE",FACE,{"disambiguationData":[OSD([sQuery(id+"F0.wireOp",EDGE,"E0"),sQuery(id+"F0.wireOp",EDGE,"E1"),sQuery(id+"F0.wireOp",EDGE,"E2"),sQuery(id+"F0.wireOp",EDGE,"E3"),sQuery(id+"F0.wireOp",EDGE,"E5")])],"isStart":true});
            cPlane(context, id + "F29", {"entities" : qUnion([Q0]), "cplaneType" : CPlaneType.OFFSET, "offset" : 5 * mm, "oppositeDirection" : true, "width" : 150 * mm, "height" : 150 * mm});
        }
        {
            var Q0;
            Q0=qCreatedBy(id+"F29.planeOp",FACE);
            var sketch = newSketch(context, id + "F30", { "sketchPlane" : qUnion([Q0])});
            skCircle(sketch, "E126.cCircle", {"center": v(60, -26.6) * mm, "radius": 2.95 * mm, "construction": true});
            skLineSegment(sketch, "E126.0", {"start": v(57.05, -24.9) * mm, "end": v(60, -23.2) * mm});
            skLineSegment(sketch, "E126.1", {"start": v(60, -23.2) * mm, "end": v(62.95, -24.9) * mm});
            skLineSegment(sketch, "E126.2", {"start": v(62.95, -24.9) * mm, "end": v(62.95, -28.3) * mm});
            skLineSegment(sketch, "E126.3", {"start": v(62.95, -28.3) * mm, "end": v(60, -30) * mm});
            skLineSegment(sketch, "E126.4", {"start": v(60, -30) * mm, "end": v(57.05, -28.3) * mm});
            skLineSegment(sketch, "E126.5", {"start": v(57.05, -28.3) * mm, "end": v(57.05, -24.9) * mm});
            skPoint(sketch, "E126.0.midPoint", {"position": v(58.52, -24.05) * mm});
            skCircle(sketch, "E127.cCircle", {"center": v(0, -26.6) * mm, "radius": 2.95 * mm, "construction": true});
            skLineSegment(sketch, "E127.0", {"start": v(-2.95, -24.9) * mm, "end": v(0, -23.2) * mm});
            skLineSegment(sketch, "E127.1", {"start": v(0, -23.2) * mm, "end": v(2.95, -24.9) * mm});
            skLineSegment(sketch, "E127.2", {"start": v(2.95, -24.9) * mm, "end": v(2.95, -28.3) * mm});
            skLineSegment(sketch, "E127.3", {"start": v(2.95, -28.3) * mm, "end": v(0, -30) * mm});
            skLineSegment(sketch, "E127.4", {"start": v(0, -30) * mm, "end": v(-2.95, -28.3) * mm});
            skLineSegment(sketch, "E127.5", {"start": v(-2.95, -28.3) * mm, "end": v(-2.95, -24.9) * mm});
            skPoint(sketch, "E127.0.midPoint", {"position": v(-1.48, -24.05) * mm});
            skCircle(sketch, "E128.cCircle", {"center": v(-60, -26.6) * mm, "radius": 2.95 * mm, "construction": true});
            skLineSegment(sketch, "E128.0", {"start": v(-62.95, -24.9) * mm, "end": v(-60, -23.2) * mm});
            skLineSegment(sketch, "E128.1", {"start": v(-60, -23.2) * mm, "end": v(-57.05, -24.9) * mm});
            skLineSegment(sketch, "E128.2", {"start": v(-57.05, -24.9) * mm, "end": v(-57.05, -28.3) * mm});
            skLineSegment(sketch, "E128.3", {"start": v(-57.05, -28.3) * mm, "end": v(-60, -30) * mm});
            skLineSegment(sketch, "E128.4", {"start": v(-60, -30) * mm, "end": v(-62.95, -28.3) * mm});
            skLineSegment(sketch, "E128.5", {"start": v(-62.95, -28.3) * mm, "end": v(-62.95, -24.9) * mm});
            skPoint(sketch, "E128.0.midPoint", {"position": v(-61.47, -24.05) * mm});
            skLineSegment(sketch, "E129.bottom", {"start": v(-62.95, -28.3) * mm, "end": v(-57.05, -28.3) * mm});
            skLineSegment(sketch, "E129.top", {"start": v(-62.95, -31.6) * mm, "end": v(-57.05, -31.6) * mm});
            skLineSegment(sketch, "E129.left", {"start": v(-62.95, -28.3) * mm, "end": v(-62.95, -31.6) * mm});
            skLineSegment(sketch, "E129.right", {"start": v(-57.05, -28.3) * mm, "end": v(-57.05, -31.6) * mm});
            skLineSegment(sketch, "E130.bottom", {"start": v(-2.95, -28.3) * mm, "end": v(2.95, -28.3) * mm});
            skLineSegment(sketch, "E130.top", {"start": v(-2.95, -31.6) * mm, "end": v(2.95, -31.6) * mm});
            skLineSegment(sketch, "E130.left", {"start": v(-2.95, -28.3) * mm, "end": v(-2.95, -31.6) * mm});
            skLineSegment(sketch, "E130.right", {"start": v(2.95, -28.3) * mm, "end": v(2.95, -31.6) * mm});
            skLineSegment(sketch, "E131.bottom", {"start": v(57.05, -28.3) * mm, "end": v(62.95, -28.3) * mm});
            skLineSegment(sketch, "E131.top", {"start": v(57.05, -31.6) * mm, "end": v(62.95, -31.6) * mm});
            skLineSegment(sketch, "E131.left", {"start": v(57.05, -28.3) * mm, "end": v(57.05, -31.6) * mm});
            skLineSegment(sketch, "E131.right", {"start": v(62.95, -28.3) * mm, "end": v(62.95, -31.6) * mm});
            skSolve(sketch);
        }
        {
            var Q0;
            Q0=qSketchRegion(id+"F30",true);
            extrude(context, id + "F31", {"entities" : qUnion([Q0]), "operationType" : NewBodyOperationType.REMOVE, "oppositeDirection" : true, "depth" : 2.8 * mm});
        }
        {
            var Q0;
            Q0=makeQuery(id+"F1.opExtrude","SWEPT_FACE",FACE,{"disambiguationData":[OSD([sQuery(id+"F0.wireOp",EDGE,"E1")])]});
            var sketch = newSketch(context, id + "F32", { "sketchPlane" : qUnion([Q0])});
            skLineSegment(sketch, "E132.bottom", {"start": v(0, -30) * mm, "end": v(-3, -30) * mm});
            skLineSegment(sketch, "E132.top", {"start": v(0, -22.5) * mm, "end": v(-3, -22.5) * mm});
            skLineSegment(sketch, "E132.left", {"start": v(0, -30) * mm, "end": v(0, -22.5) * mm});
            skLineSegment(sketch, "E132.right", {"start": v(-3, -30) * mm, "end": v(-3, -22.5) * mm});
            skSolve(sketch);
        }
        {
            var Q0;
            Q0=makeQuery(id+"F1.opExtrude","CAP_EDGE",EDGE,{"disambiguationData":[OSD([sQuery(id+"F0.wireOp",EDGE,"E0")])],"isStart":true});
            var Q1;
            Q1=makeQuery(id+"F1.opExtrude","CAP_EDGE",EDGE,{"disambiguationData":[OSD([sQuery(id+"F0.wireOp",EDGE,"E1")])],"isStart":true});
            var Q2;
            Q2=makeQuery(id+"F1.opExtrude","SWEPT_EDGE",EDGE,{"disambiguationData":[OSD([sQuery(id+"F0.wireOp",EDGE,"E0"),sQuery(id+"F0.wireOp",EDGE,"E1")])]});
            var Q3;
            Q3=makeQuery(id+"F1.opExtrude","SWEPT_EDGE",EDGE,{"disambiguationData":[OSD([sQuery(id+"F0.wireOp",EDGE,"E2"),sQuery(id+"F0.wireOp",EDGE,"E3")])]});
            var Q4;
            Q4=makeQuery(id+"F1.opExtrude","SWEPT_EDGE",EDGE,{"disambiguationData":[OSD([sQuery(id+"F0.wireOp",EDGE,"E0"),sQuery(id+"F0.wireOp",EDGE,"E5")])]});
            var Q5;
            Q5=makeQuery(id+"F1.opExtrude","CAP_EDGE",EDGE,{"disambiguationData":[OSD([sQuery(id+"F0.wireOp",EDGE,"E3"),sQuery(id+"F0.wireOp",EDGE,"E5")])],"isStart":true});
            fillet(context, id + "F33", {"entities" : qUnion([Q0, Q1, Q2, Q3, Q4, Q5]), "radius" : 4 * mm, "tangentPropagation" : true, "allowEdgeOverflow" : false});
        }
        {
            var Q0;
            Q0=makeQuery(id+"F25.boolean.opBoolean","INTERSECT",EDGE,{"derivedFrom":[makeQuery(id+"F10.boolean.opBoolean","MERGE",FACE,{"derivedFrom":[makeQuery(id+"F1.opExtrude","SWEPT_FACE",FACE,{"disambiguationData":[OSD([sQuery(id+"F0.wireOp",EDGE,"E0")])]}),makeQuery(id+"F10.opExtrude","CAP_FACE",FACE,{"disambiguationData":[OSD([sQuery(id+"F9.wireOp",EDGE,"093ffe32-b858-4e39-8033-2af8f1862302"),sQuery(id+"F9.wireOp",EDGE,"6615f876-654d-472b-932f-aa817a99cf8c"),sQuery(id+"F9.wireOp",EDGE,"880e6486-e846-4002-b9b7-1cb835c84523"),sQuery(id+"F9.wireOp",EDGE,"7e94aab6-89b0-44ac-a5a2-104160a8799a"),sQuery(id+"F9.wireOp",EDGE,"5bf2236a-818f-4daa-bb11-a80a7fe0e66a"),sQuery(id+"F9.wireOp",EDGE,"dcff3f73-e1ff-4264-9410-abdb107e6245"),sQuery(id+"F9.wireOp",EDGE,"66e4b800-3c0e-4def-9d8a-5724071b2d4d"),sQuery(id+"F9.wireOp",EDGE,"07cf7429-5678-4c4a-b063-5e15791e93b6"),sQuery(id+"F9.wireOp",EDGE,"e1dbcd6d-4689-40e3-8967-04de52220fc4"),sQuery(id+"F9.wireOp",EDGE,"f96e3a45-2d0c-4d7f-8c63-5261d2a80a69.6.MirrorCS"),sQuery(id+"F9.wireOp",EDGE,"f96e3a45-2d0c-4d7f-8c63-5261d2a80a69.10.MirrorCS"),sQuery(id+"F9.wireOp",EDGE,"f96e3a45-2d0c-4d7f-8c63-5261d2a80a69.15.MirrorCS"),sQuery(id+"F9.wireOp",EDGE,"f96e3a45-2d0c-4d7f-8c63-5261d2a80a69.19.MirrorCS"),sQuery(id+"F9.wireOp",EDGE,"f96e3a45-2d0c-4d7f-8c63-5261d2a80a69.20.MirrorCS"),sQuery(id+"F9.wireOp",EDGE,"f96e3a45-2d0c-4d7f-8c63-5261d2a80a69.22.MirrorCS"),sQuery(id+"F9.wireOp",EDGE,"f96e3a45-2d0c-4d7f-8c63-5261d2a80a69.23.MirrorCS"),sQuery(id+"F9.wireOp",EDGE,"f96e3a45-2d0c-4d7f-8c63-5261d2a80a69.26.MirrorCS"),sQuery(id+"F9.wireOp",EDGE,"f96e3a45-2d0c-4d7f-8c63-5261d2a80a69.27.MirrorCS")])],"isStart":false}),makeQuery(id+"F10.opExtrude","CAP_FACE",FACE,{"disambiguationData":[OSD([sQuery(id+"F9.wireOp",EDGE,"d48beb5c-8eb7-4b5d-91d8-b103da09848f.8.MirrorCS"),sQuery(id+"F9.wireOp",EDGE,"d48beb5c-8eb7-4b5d-91d8-b103da09848f.12.MirrorCS"),sQuery(id+"F9.wireOp",EDGE,"d48beb5c-8eb7-4b5d-91d8-b103da09848f.22.MirrorCS"),sQuery(id+"F9.wireOp",EDGE,"d48beb5c-8eb7-4b5d-91d8-b103da09848f.31.MirrorCS"),sQuery(id+"F9.wireOp",EDGE,"d48beb5c-8eb7-4b5d-91d8-b103da09848f.38.MirrorCS"),sQuery(id+"F9.wireOp",EDGE,"d48beb5c-8eb7-4b5d-91d8-b103da09848f.42.MirrorCS"),sQuery(id+"F9.wireOp",EDGE,"d48beb5c-8eb7-4b5d-91d8-b103da09848f.43.MirrorCS"),sQuery(id+"F9.wireOp",EDGE,"d48beb5c-8eb7-4b5d-91d8-b103da09848f.46.MirrorCS"),sQuery(id+"F9.wireOp",EDGE,"d48beb5c-8eb7-4b5d-91d8-b103da09848f.51.MirrorCS"),sQuery(id+"F9.wireOp",EDGE,"d48beb5c-8eb7-4b5d-91d8-b103da09848f.53.MirrorCS"),sQuery(id+"F9.wireOp",EDGE,"d48beb5c-8eb7-4b5d-91d8-b103da09848f.55.MirrorCS"),sQuery(id+"F9.wireOp",EDGE,"d48beb5c-8eb7-4b5d-91d8-b103da09848f.56.MirrorCS"),sQuery(id+"F9.wireOp",EDGE,"d48beb5c-8eb7-4b5d-91d8-b103da09848f.57.MirrorCS"),sQuery(id+"F9.wireOp",EDGE,"d48beb5c-8eb7-4b5d-91d8-b103da09848f.58.MirrorCS"),sQuery(id+"F9.wireOp",EDGE,"d48beb5c-8eb7-4b5d-91d8-b103da09848f.59.MirrorCS"),sQuery(id+"F9.wireOp",EDGE,"d48beb5c-8eb7-4b5d-91d8-b103da09848f.60.MirrorCS"),sQuery(id+"F9.wireOp",EDGE,"d48beb5c-8eb7-4b5d-91d8-b103da09848f.62.MirrorCS"),sQuery(id+"F9.wireOp",EDGE,"d48beb5c-8eb7-4b5d-91d8-b103da09848f.63.MirrorCS")])],"isStart":false})]}),makeQuery(id+"F25.opExtrude","SWEPT_FACE",FACE,{"disambiguationData":[OSD([sQuery(id+"F24.wireOp",EDGE,"E115.right")])]})]});
            fillet(context, id + "F34", {"entities" : qUnion([Q0]), "radius" : 1.5 * mm, "tangentPropagation" : true, "allowEdgeOverflow" : false});
        }
        {
            var Q0;
            Q0=makeQuery(id+"F1.opExtrude","SWEPT_FACE",FACE,{"disambiguationData":[OSD([sQuery(id+"F0.wireOp",EDGE,"E3"),sQuery(id+"F0.wireOp",EDGE,"E5")])]});
            cPlane(context, id + "F35", {"entities" : qUnion([Q0]), "cplaneType" : CPlaneType.OFFSET, "offset" : 5 * mm, "oppositeDirection" : true, "width" : 150 * mm, "height" : 150 * mm});
        }
        {
            var Q0;
            Q0=qCreatedBy(id+"F35.planeOp",FACE);
            var sketch = newSketch(context, id + "F36", { "sketchPlane" : qUnion([Q0])});
            skCircle(sketch, "E133.cCircle", {"center": v(25, -20) * mm, "radius": 2.95 * mm, "construction": true});
            skLineSegment(sketch, "E133.0", {"start": v(27.95, -18.3) * mm, "end": v(27.95, -21.7) * mm});
            skLineSegment(sketch, "E133.1", {"start": v(27.95, -21.7) * mm, "end": v(25, -23.4) * mm});
            skLineSegment(sketch, "E133.2", {"start": v(25, -23.4) * mm, "end": v(22.05, -21.7) * mm});
            skLineSegment(sketch, "E133.3", {"start": v(22.05, -21.7) * mm, "end": v(22.05, -18.3) * mm});
            skLineSegment(sketch, "E133.4", {"start": v(22.05, -18.3) * mm, "end": v(25, -16.6) * mm});
            skLineSegment(sketch, "E133.5", {"start": v(25, -16.6) * mm, "end": v(27.95, -18.3) * mm});
            skPoint(sketch, "E133.0.midPoint", {"position": v(27.95, -20) * mm});
            skLineSegment(sketch, "E134.bottom", {"start": v(22.05, -21.7) * mm, "end": v(27.95, -21.7) * mm});
            skLineSegment(sketch, "E135.bottom", {"start": v(27.95, -21.7) * mm, "end": v(22.05, -21.7) * mm});
            skLineSegment(sketch, "E135.top", {"start": v(27.95, -30) * mm, "end": v(22.05, -30) * mm});
            skLineSegment(sketch, "E135.left", {"start": v(27.95, -21.7) * mm, "end": v(27.95, -30) * mm});
            skLineSegment(sketch, "E135.right", {"start": v(22.05, -21.7) * mm, "end": v(22.05, -30) * mm});
            skCircle(sketch, "E136.cCircle", {"center": v(45, 5) * mm, "radius": 2.95 * mm, "construction": true});
            skLineSegment(sketch, "E136.0", {"start": v(42.05, 3.3) * mm, "end": v(42.05, 6.7) * mm});
            skLineSegment(sketch, "E136.1", {"start": v(42.05, 6.7) * mm, "end": v(45, 8.4) * mm});
            skLineSegment(sketch, "E136.2", {"start": v(45, 8.4) * mm, "end": v(47.95, 6.7) * mm});
            skLineSegment(sketch, "E136.3", {"start": v(47.95, 6.7) * mm, "end": v(47.95, 3.3) * mm});
            skLineSegment(sketch, "E136.4", {"start": v(47.95, 3.3) * mm, "end": v(45, 1.6) * mm});
            skLineSegment(sketch, "E136.5", {"start": v(45, 1.6) * mm, "end": v(42.05, 3.3) * mm});
            skPoint(sketch, "E136.0.midPoint", {"position": v(42.05, 5) * mm});
            skLineSegment(sketch, "E137.bottom", {"start": v(42.05, 3.3) * mm, "end": v(47.95, 3.3) * mm});
            skLineSegment(sketch, "E137.top", {"start": v(42.05, -5) * mm, "end": v(47.95, -5) * mm});
            skLineSegment(sketch, "E137.left", {"start": v(42.05, 3.3) * mm, "end": v(42.05, -5) * mm});
            skLineSegment(sketch, "E137.right", {"start": v(47.95, 3.3) * mm, "end": v(47.95, -5) * mm});
            skSolve(sketch);
        }
        {
            var Q0;
            Q0=qSketchRegion(id+"F36",true);
            extrude(context, id + "F37", {"entities" : qUnion([Q0]), "operationType" : NewBodyOperationType.REMOVE, "oppositeDirection" : true, "depth" : 2.8 * mm});
        }
        {
            var Q0;
            Q0=makeQuery(id+"F1.opExtrude","SWEPT_FACE",FACE,{"disambiguationData":[OSD([sQuery(id+"F0.wireOp",EDGE,"E3"),sQuery(id+"F0.wireOp",EDGE,"E5")])]});
            var sketch = newSketch(context, id + "F38", { "sketchPlane" : qUnion([Q0])});
            skCircle(sketch, "E138", {"center": v(25, -20) * mm, "radius": 1.65 * mm});
            skCircle(sketch, "E139", {"center": v(45, 5) * mm, "radius": 1.65 * mm});
            skSolve(sketch);
        }
        {
            var Q0;
            Q0=qSketchRegion(id+"F38",true);
            extrude(context, id + "F39", {"entities" : qUnion([Q0]), "operationType" : NewBodyOperationType.REMOVE, "oppositeDirection" : true, "depth" : 15 * mm});
        }
        {
            var Q0;
            Q0=qSketchRegion(id+"F32",true);
            extrude(context, id + "F40", {"entities" : qUnion([Q0]), "operationType" : NewBodyOperationType.REMOVE, "endBound" : BoundingType.THROUGH_ALL, "oppositeDirection" : true, "depth" : 15 * mm});
        }
        {
            var Q0;
            {var subQ0=makeQuery(id+"F1.opExtrude","SWEPT_FACE",FACE,{"disambiguationData":[OSD([sQuery(id+"F0.wireOp",EDGE,"E0")])]});var subQ1=makeQuery(id+"F7.opExtrude","SWEPT_FACE",FACE,{"disambiguationData":[OSD([sQuery(id+"F6.wireOp",EDGE,"E11")])]});var subQ3=sQuery(id+"F9.wireOp",EDGE,"E36.MirrorCS");Q0=makeQuery(id+"F10.boolean.opBoolean","SPLIT",EDGE,{"disambiguationData":[TD([makeQuery(id+"F10.opExtrude","SWEPT_FACE",FACE,{"disambiguationData":[OSD([subQ3])]})])],"derivedFrom":makeQuery(id+"F7.boolean.opBoolean","INTERSECT",EDGE,{"derivedFrom":[subQ0,subQ1]})});}
            var Q1;
            {var subQ0=makeQuery(id+"F1.opExtrude","SWEPT_FACE",FACE,{"disambiguationData":[OSD([sQuery(id+"F0.wireOp",EDGE,"E0")])]});var subQ1=makeQuery(id+"F7.opExtrude","SWEPT_FACE",FACE,{"disambiguationData":[OSD([sQuery(id+"F6.wireOp",EDGE,"E11")])]});var subQ3=sQuery(id+"F9.wireOp",EDGE,"E29");Q1=makeQuery(id+"F10.boolean.opBoolean","SPLIT",EDGE,{"disambiguationData":[TD([makeQuery(id+"F10.opExtrude","SWEPT_FACE",FACE,{"disambiguationData":[OSD([subQ3])]})])],"derivedFrom":makeQuery(id+"F7.boolean.opBoolean","INTERSECT",EDGE,{"derivedFrom":[subQ0,subQ1]})});}
            var Q2;
            {var subQ0=makeQuery(id+"F1.opExtrude","SWEPT_FACE",FACE,{"disambiguationData":[OSD([sQuery(id+"F0.wireOp",EDGE,"E0")])]});var subQ1=makeQuery(id+"F7.opExtrude","SWEPT_FACE",FACE,{"disambiguationData":[OSD([sQuery(id+"F6.wireOp",EDGE,"E11")])]});var subQ3=sQuery(id+"F9.wireOp",EDGE,"E38.MirrorCS");Q2=makeQuery(id+"F10.boolean.opBoolean","SPLIT",EDGE,{"disambiguationData":[TD([makeQuery(id+"F10.opExtrude","SWEPT_FACE",FACE,{"disambiguationData":[OSD([subQ3])]})])],"derivedFrom":makeQuery(id+"F7.boolean.opBoolean","INTERSECT",EDGE,{"derivedFrom":[subQ0,subQ1]})});}
            var Q3;
            {var subQ0=makeQuery(id+"F1.opExtrude","SWEPT_FACE",FACE,{"disambiguationData":[OSD([sQuery(id+"F0.wireOp",EDGE,"E0")])]});var subQ1=makeQuery(id+"F7.opExtrude","SWEPT_FACE",FACE,{"disambiguationData":[OSD([sQuery(id+"F6.wireOp",EDGE,"E11")])]});var subQ3=sQuery(id+"F9.wireOp",EDGE,"E28");Q3=makeQuery(id+"F10.boolean.opBoolean","SPLIT",EDGE,{"disambiguationData":[TD([makeQuery(id+"F10.opExtrude","SWEPT_FACE",FACE,{"disambiguationData":[OSD([subQ3])]})])],"derivedFrom":makeQuery(id+"F7.boolean.opBoolean","INTERSECT",EDGE,{"derivedFrom":[subQ0,subQ1]})});}
            var Q4;
            {var subQ0=makeQuery(id+"F1.opExtrude","SWEPT_FACE",FACE,{"disambiguationData":[OSD([sQuery(id+"F0.wireOp",EDGE,"E0")])]});var subQ1=makeQuery(id+"F7.opExtrude","SWEPT_FACE",FACE,{"disambiguationData":[OSD([sQuery(id+"F6.wireOp",EDGE,"E10")])]});var subQ3=sQuery(id+"F9.wireOp",EDGE,"E61.MirrorCS");Q4=makeQuery(id+"F10.boolean.opBoolean","SPLIT",EDGE,{"disambiguationData":[TD([makeQuery(id+"F10.opExtrude","SWEPT_FACE",FACE,{"disambiguationData":[OSD([subQ3])]})])],"derivedFrom":makeQuery(id+"F7.boolean.opBoolean","INTERSECT",EDGE,{"derivedFrom":[subQ0,subQ1]})});}
            var Q5;
            {var subQ0=makeQuery(id+"F1.opExtrude","SWEPT_FACE",FACE,{"disambiguationData":[OSD([sQuery(id+"F0.wireOp",EDGE,"E0")])]});var subQ1=makeQuery(id+"F7.opExtrude","SWEPT_FACE",FACE,{"disambiguationData":[OSD([sQuery(id+"F6.wireOp",EDGE,"E10")])]});var subQ2=sQuery(id+"F9.wireOp",EDGE,"E60.MirrorCS");Q5=makeQuery(id+"F10.boolean.opBoolean","SPLIT",EDGE,{"disambiguationData":[TD([makeQuery(id+"F10.opExtrude","SWEPT_FACE",FACE,{"disambiguationData":[OSD([subQ2])]})])],"derivedFrom":makeQuery(id+"F7.boolean.opBoolean","INTERSECT",EDGE,{"derivedFrom":[subQ0,subQ1]})});}
            var Q6;
            {var subQ0=makeQuery(id+"F1.opExtrude","SWEPT_FACE",FACE,{"disambiguationData":[OSD([sQuery(id+"F0.wireOp",EDGE,"E0")])]});var subQ1=makeQuery(id+"F7.opExtrude","SWEPT_FACE",FACE,{"disambiguationData":[OSD([sQuery(id+"F6.wireOp",EDGE,"E10")])]});var subQ2=sQuery(id+"F9.wireOp",EDGE,"E57.MirrorCS");Q6=makeQuery(id+"F10.boolean.opBoolean","SPLIT",EDGE,{"disambiguationData":[TD([makeQuery(id+"F10.opExtrude","SWEPT_FACE",FACE,{"disambiguationData":[OSD([subQ2])]})])],"derivedFrom":makeQuery(id+"F7.boolean.opBoolean","INTERSECT",EDGE,{"derivedFrom":[subQ0,subQ1]})});}
            var Q7;
            {var subQ0=makeQuery(id+"F1.opExtrude","SWEPT_FACE",FACE,{"disambiguationData":[OSD([sQuery(id+"F0.wireOp",EDGE,"E0")])]});var subQ1=makeQuery(id+"F7.opExtrude","SWEPT_FACE",FACE,{"disambiguationData":[OSD([sQuery(id+"F6.wireOp",EDGE,"E10")])]});var subQ3=sQuery(id+"F9.wireOp",EDGE,"E65.MirrorCS");Q7=makeQuery(id+"F10.boolean.opBoolean","SPLIT",EDGE,{"disambiguationData":[TD([makeQuery(id+"F10.opExtrude","SWEPT_FACE",FACE,{"disambiguationData":[OSD([subQ3])]})])],"derivedFrom":makeQuery(id+"F7.boolean.opBoolean","INTERSECT",EDGE,{"derivedFrom":[subQ0,subQ1]})});}
            fillet(context, id + "F41", {"entities" : qUnion([Q0, Q1, Q2, Q3, Q4, Q5, Q6, Q7]), "radius" : 3 * mm, "tangentPropagation" : true, "allowEdgeOverflow" : false});
        }
        {
            var Q0;
            Q0=makeQuery(id+"F1.opExtrude","SWEPT_BODY",BODY,{"disambiguationData":[OSD([sQuery(id+"F0.wireOp",EDGE,"E0"),sQuery(id+"F0.wireOp",EDGE,"E1"),sQuery(id+"F0.wireOp",EDGE,"E2"),sQuery(id+"F0.wireOp",EDGE,"E3"),sQuery(id+"F0.wireOp",EDGE,"E4"),sQuery(id+"F0.wireOp",EDGE,"E5")])]});
            var Q1;
            Q1=makeQuery(id+"F1.opExtrude","CAP_FACE",FACE,{"disambiguationData":[OSD([sQuery(id+"F0.wireOp",EDGE,"E0"),sQuery(id+"F0.wireOp",EDGE,"E1"),sQuery(id+"F0.wireOp",EDGE,"E2"),sQuery(id+"F0.wireOp",EDGE,"E3"),sQuery(id+"F0.wireOp",EDGE,"E4"),sQuery(id+"F0.wireOp",EDGE,"E5")])],"isStart":false});
            mirror(context, id + "F42", {"operationType" : NewBodyOperationType.ADD, "entities" : qUnion([Q0]), "mirrorPlane" : qUnion([Q1])});
        }
    });
